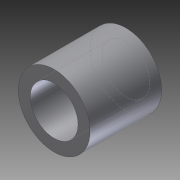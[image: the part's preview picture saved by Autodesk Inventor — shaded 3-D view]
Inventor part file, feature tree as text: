
AUTODESK INVENTOR PART (.ipt)
format: ipt  version: 2012 (Build 160160000, 160)  size: 84,480 bytes
history: native  units: in
note: dims shown in document units (in); Inventor stores cm internally (conversion verified against a paired STEP export)
features: extrude x1, sketch x1
ambient origin geometry x8: Origin, YZ Plane, XZ Plane, XY Plane, X Axis, Y Axis, Z Axis, Center Point
bodies: Solid1 (feature_tree)
feature tree (2):
  extrude  "Extrusion1"  Depth=0.375in
  sketch  "Sketch1"  dims[d0=0.25in d2=0.375in d3=0.5in d4=0.0in]
